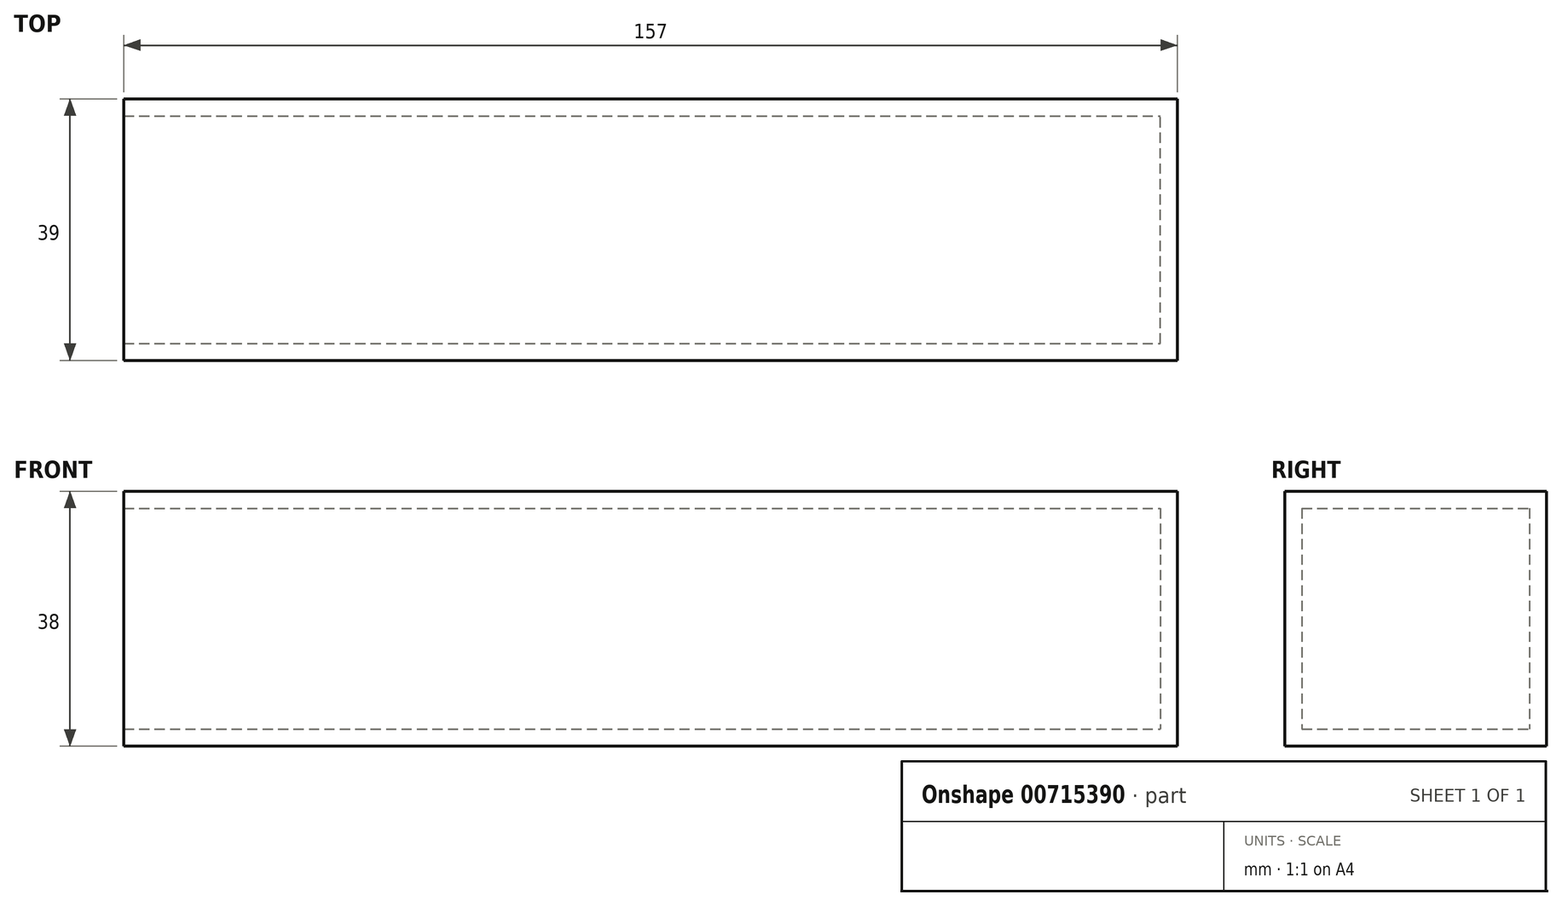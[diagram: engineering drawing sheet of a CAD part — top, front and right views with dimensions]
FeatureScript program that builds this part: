
annotation { "Feature Type Name" : "Feature", "Feature Type Description" : "" }
export const myFeature = defineFeature(function(context is Context, id is Id, definition is map)
    precondition{}
    {
        {
            var Q0;
            Q0=qCreatedBy(makeId("Front.planeOp"),FACE);
            var sketch = newSketch(context, id + "F0", { "sketchPlane" : qUnion([Q0])});
            skLineSegment(sketch, "E0.bottom", {"start": v(-157, 38) * mm, "end": v(0, 38) * mm});
            skLineSegment(sketch, "E0.top", {"start": v(-157, 0) * mm, "end": v(0, 0) * mm});
            skLineSegment(sketch, "E0.left", {"start": v(-157, 38) * mm, "end": v(-157, 0) * mm});
            skLineSegment(sketch, "E0.right", {"start": v(0, 38) * mm, "end": v(0, 0) * mm});
            skSolve(sketch);
        }
        {
            var Q0;
            Q0 = qSketchRegion(id + "F0", true);
            extrude(context, id + "F1", {"entities" : qUnion([Q0]), "depth" : 39 * mm, "offsetDistance" : 25.4 * mm});
        }
        {
            var Q0;
            Q0=makeQuery(id+"F1.opExtrude","SWEPT_FACE",FACE,{"disambiguationData":[OSD([sQuery(id+"F0.wireOp",EDGE,"E0.left")])]});
            shell(context, id + "F2", {"entities" : qUnion([Q0]), "thickness" : 2.54 * mm});
        }
    });
